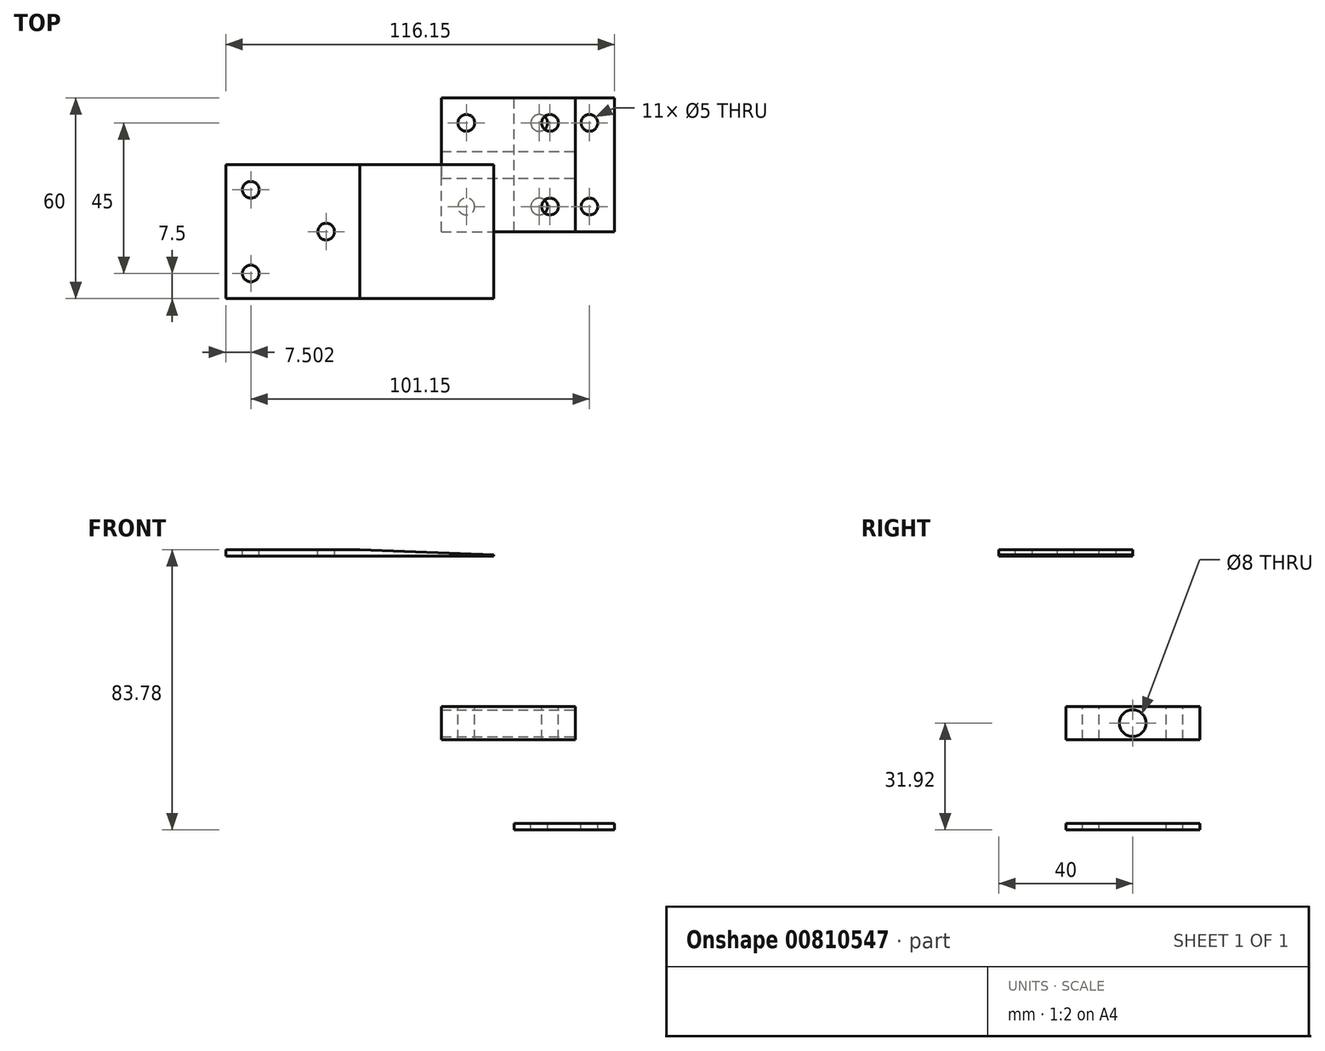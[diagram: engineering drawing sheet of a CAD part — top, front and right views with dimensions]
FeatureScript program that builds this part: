
annotation { "Feature Type Name" : "Feature", "Feature Type Description" : "" }
export const myFeature = defineFeature(function(context is Context, id is Id, definition is map)
    precondition{}
    {
        {
            var Q0;
            Q0=qCreatedBy(makeId("Front.planeOp"),FACE);
            var sketch = newSketch(context, id + "F0", { "sketchPlane" : qUnion([Q0])});
            skLineSegment(sketch, "E0.bottom", {"start": v(-20, 5) * mm, "end": v(20, 5) * mm});
            skLineSegment(sketch, "E0.top", {"start": v(-20, -5) * mm, "end": v(20, -5) * mm});
            skLineSegment(sketch, "E0.left", {"start": v(-20, 5) * mm, "end": v(-20, -5) * mm});
            skLineSegment(sketch, "E0.right", {"start": v(20, 5) * mm, "end": v(20, -5) * mm});
            skPoint(sketch, "E0.middle", {"position": v(0, 0) * mm});
            skSolve(sketch);
        }
        {
            var Q0;
            Q0=makeQuery(id+"F0.imprint","IMPRINT",FACE,{"disambiguationData":[TD([[makeQuery(id+"F0.imprint","IMPRINT",EDGE,{"derivedFrom":sQuery(id+"F0.wireOp",EDGE,"E0.bottom")}),-1.0]])]});
            extrude(context, id + "F1", {"entities" : qUnion([Q0]), "endBound" : BoundingType.SYMMETRIC, "depth" : 40 * mm, "offsetDistance" : 25.4 * mm});
        }
        {
            var Q0;
            Q0=makeQuery(id+"F1.opExtrude","SWEPT_FACE",FACE,{"disambiguationData":[OSD([sQuery(id+"F0.wireOp",EDGE,"E0.right")])]});
            var sketch = newSketch(context, id + "F2", { "sketchPlane" : qUnion([Q0])});
            skPoint(sketch, "E1", {"position": v(0, 0) * mm});
            skSolve(sketch);
        }
        {
            var Q0;
            Q0=sQuery(id+"F2.wireOp",VERTEX,"E1");
            var Q1;
            Q1=makeQuery(id+"F1.opExtrude","SWEPT_BODY",BODY,{"disambiguationData":[OSD([sQuery(id+"F0.wireOp",EDGE,"E0.bottom"),sQuery(id+"F0.wireOp",EDGE,"E0.top"),sQuery(id+"F0.wireOp",EDGE,"E0.left"),sQuery(id+"F0.wireOp",EDGE,"E0.right")])]});
            hole(context, id + "F3", {"style" : HoleStyle.SIMPLE, "endStyle" : HoleEndStyle.THROUGH, "holeDiameter" : 8 * mm, "majorDiameter" : 6.35 * mm, "isTappedThrough" : true, "tappedDepth" : 12.7 * mm, "tapClearance" : 3, "locations" : qUnion([Q0]), "scope" : qUnion([Q1])});
        }
        {
            var Q0;
            Q0=makeQuery(id+"F1.opExtrude","SWEPT_FACE",FACE,{"disambiguationData":[OSD([sQuery(id+"F0.wireOp",EDGE,"E0.bottom")])]});
            var sketch = newSketch(context, id + "F4", { "sketchPlane" : qUnion([Q0])});
            skLineSegment(sketch, "E2.bottom", {"start": v(-12.5, 12.5) * mm, "end": v(12.5, 12.5) * mm});
            skLineSegment(sketch, "E2.top", {"start": v(-12.5, -12.5) * mm, "end": v(12.5, -12.5) * mm});
            skLineSegment(sketch, "E2.left", {"start": v(-12.5, 12.5) * mm, "end": v(-12.5, -12.5) * mm});
            skLineSegment(sketch, "E2.right", {"start": v(12.5, 12.5) * mm, "end": v(12.5, -12.5) * mm});
            skPoint(sketch, "E2.middle", {"position": v(0, 0) * mm});
            skSolve(sketch);
        }
        {
            var Q0;
            Q0=sQuery(id+"F4.wireOp",VERTEX,"E2.bottom.end");
            var Q1;
            Q1=sQuery(id+"F4.wireOp",VERTEX,"E2.bottom.start");
            var Q2;
            Q2=sQuery(id+"F4.wireOp",VERTEX,"E2.top.start");
            var Q3;
            Q3=sQuery(id+"F4.wireOp",VERTEX,"E2.top.end");
            var Q4;
            Q4=makeQuery(id+"F1.opExtrude","SWEPT_BODY",BODY,{"disambiguationData":[OSD([sQuery(id+"F0.wireOp",EDGE,"E0.bottom"),sQuery(id+"F0.wireOp",EDGE,"E0.top"),sQuery(id+"F0.wireOp",EDGE,"E0.left"),sQuery(id+"F0.wireOp",EDGE,"E0.right")])]});
            hole(context, id + "F5", {"style" : HoleStyle.SIMPLE, "endStyle" : HoleEndStyle.THROUGH, "holeDiameter" : 5 * mm, "majorDiameter" : 5 * mm, "isTappedThrough" : true, "tappedDepth" : 12.7 * mm, "tapClearance" : 3, "locations" : qUnion([Q0, Q1, Q2, Q3]), "scope" : qUnion([Q4])});
        }
        {
            var Q0;
            Q0=qCreatedBy(makeId("Front.planeOp"),FACE);
            var sketch = newSketch(context, id + "F6", { "sketchPlane" : qUnion([Q0])});
            skLineSegment(sketch, "E3.bottom", {"start": v(1.77, -29.92) * mm, "end": v(31.77, -29.92) * mm});
            skLineSegment(sketch, "E3.top", {"start": v(1.77, -31.92) * mm, "end": v(31.77, -31.92) * mm});
            skLineSegment(sketch, "E3.left", {"start": v(1.77, -29.92) * mm, "end": v(1.77, -31.92) * mm});
            skLineSegment(sketch, "E3.right", {"start": v(31.77, -29.92) * mm, "end": v(31.77, -31.92) * mm});
            skSolve(sketch);
        }
        {
            var Q0;
            Q0 = qSketchRegion(id + "F6", true);
            extrude(context, id + "F7", {"entities" : qUnion([Q0]), "endBound" : BoundingType.SYMMETRIC, "depth" : 40 * mm, "offsetDistance" : 25 * mm});
        }
        {
            var Q0;
            Q0=makeQuery(id+"F7.opExtrude","SWEPT_FACE",FACE,{"disambiguationData":[OSD([sQuery(id+"F6.wireOp",EDGE,"E3.bottom")])]});
            var sketch = newSketch(context, id + "F8", { "sketchPlane" : qUnion([Q0])});
            skLineSegment(sketch, "E4.bottom", {"start": v(24.27, 12.5) * mm, "end": v(9.27, 12.5) * mm});
            skLineSegment(sketch, "E4.top", {"start": v(24.27, -12.5) * mm, "end": v(9.27, -12.5) * mm});
            skLineSegment(sketch, "E4.left", {"start": v(24.27, 12.5) * mm, "end": v(24.27, -12.5) * mm});
            skLineSegment(sketch, "E4.right", {"start": v(9.27, 12.5) * mm, "end": v(9.27, -12.5) * mm});
            skPoint(sketch, "E4.middle", {"position": v(16.77, 0) * mm});
            skSolve(sketch);
        }
        {
            var Q0;
            Q0=sQuery(id+"F8.wireOp",VERTEX,"E4.bottom.end");
            var Q1;
            Q1=sQuery(id+"F8.wireOp",VERTEX,"E4.top.end");
            var Q2;
            Q2=sQuery(id+"F8.wireOp",VERTEX,"E4.top.start");
            var Q3;
            Q3=sQuery(id+"F8.wireOp",VERTEX,"E4.bottom.start");
            var Q4;
            Q4=makeQuery(id+"F7.opExtrude","SWEPT_BODY",BODY,{"disambiguationData":[OSD([sQuery(id+"F6.wireOp",EDGE,"E3.bottom"),sQuery(id+"F6.wireOp",EDGE,"E3.top"),sQuery(id+"F6.wireOp",EDGE,"E3.left"),sQuery(id+"F6.wireOp",EDGE,"E3.right")])]});
            hole(context, id + "F9", {"style" : HoleStyle.SIMPLE, "endStyle" : HoleEndStyle.THROUGH, "holeDiameter" : 5 * mm, "majorDiameter" : 5 * mm, "isTappedThrough" : true, "tappedDepth" : 12.7 * mm, "tapClearance" : 3, "locations" : qUnion([Q0, Q1, Q2, Q3]), "scope" : qUnion([Q4])});
        }
        {
            var Q0;
            Q0=qCreatedBy(makeId("Front.planeOp"),FACE);
            var sketch = newSketch(context, id + "F10", { "sketchPlane" : qUnion([Q0])});
            skLineSegment(sketch, "E5.bottom", {"start": v(-44.38, 49.86) * mm, "end": v(-84.38, 49.86) * mm});
            skLineSegment(sketch, "E5.top", {"start": v(-44.38, 51.86) * mm, "end": v(-84.38, 51.86) * mm});
            skLineSegment(sketch, "E5.left", {"start": v(-44.38, 49.86) * mm, "end": v(-44.38, 51.86) * mm});
            skLineSegment(sketch, "E5.right", {"start": v(-84.38, 49.86) * mm, "end": v(-84.38, 51.86) * mm});
            skPoint(sketch, "E5.middle", {"position": v(-64.38, 50.86) * mm});
            skLineSegment(sketch, "E6", {"start": v(-44.38, 49.86) * mm, "end": v(-4.38, 49.86) * mm});
            skLineSegment(sketch, "E7", {"start": v(-4.38, 49.86) * mm, "end": v(-4.38, 50.36) * mm});
            skLineSegment(sketch, "E8", {"start": v(-4.38, 50.36) * mm, "end": v(-44.38, 51.86) * mm});
            skSolve(sketch);
        }
        {
            var Q0;
            Q0 = qSketchRegion(id + "F10", true);
            extrude(context, id + "F11", {"entities" : qUnion([Q0]), "depth" : 40 * mm, "offsetDistance" : 25 * mm});
        }
        {
            var Q0;
            Q0=makeQuery(id+"F11.opExtrude","SWEPT_FACE",FACE,{"disambiguationData":[OSD([sQuery(id+"F10.wireOp",EDGE,"E5.top")])]});
            var sketch = newSketch(context, id + "F12", { "sketchPlane" : qUnion([Q0])});
            skLineSegment(sketch, "E9", {"start": v(-76.88, -32.5) * mm, "end": v(-76.88, -7.5) * mm});
            skPoint(sketch, "E10", {"position": v(-54.38, -20) * mm});
            skSolve(sketch);
        }
        {
            var Q0;
            Q0=sQuery(id+"F12.wireOp",VERTEX,"E9.end");
            var Q1;
            Q1=sQuery(id+"F12.wireOp",VERTEX,"E9.start");
            var Q2;
            Q2=sQuery(id+"F12.wireOp",VERTEX,"E10");
            var Q3;
            Q3=makeQuery(id+"F11.opExtrude","SWEPT_BODY",BODY,{"disambiguationData":[OSD([sQuery(id+"F10.wireOp",EDGE,"E5.bottom"),sQuery(id+"F10.wireOp",EDGE,"E5.top"),sQuery(id+"F10.wireOp",EDGE,"E5.right"),sQuery(id+"F10.wireOp",EDGE,"E6"),sQuery(id+"F10.wireOp",EDGE,"E7"),sQuery(id+"F10.wireOp",EDGE,"E8")])]});
            hole(context, id + "F13", {"style" : HoleStyle.SIMPLE, "endStyle" : HoleEndStyle.THROUGH, "holeDiameter" : 5 * mm, "majorDiameter" : 5 * mm, "isTappedThrough" : true, "tappedDepth" : 12.7 * mm, "tapClearance" : 3, "locations" : qUnion([Q0, Q1, Q2]), "scope" : qUnion([Q3])});
        }
    });
